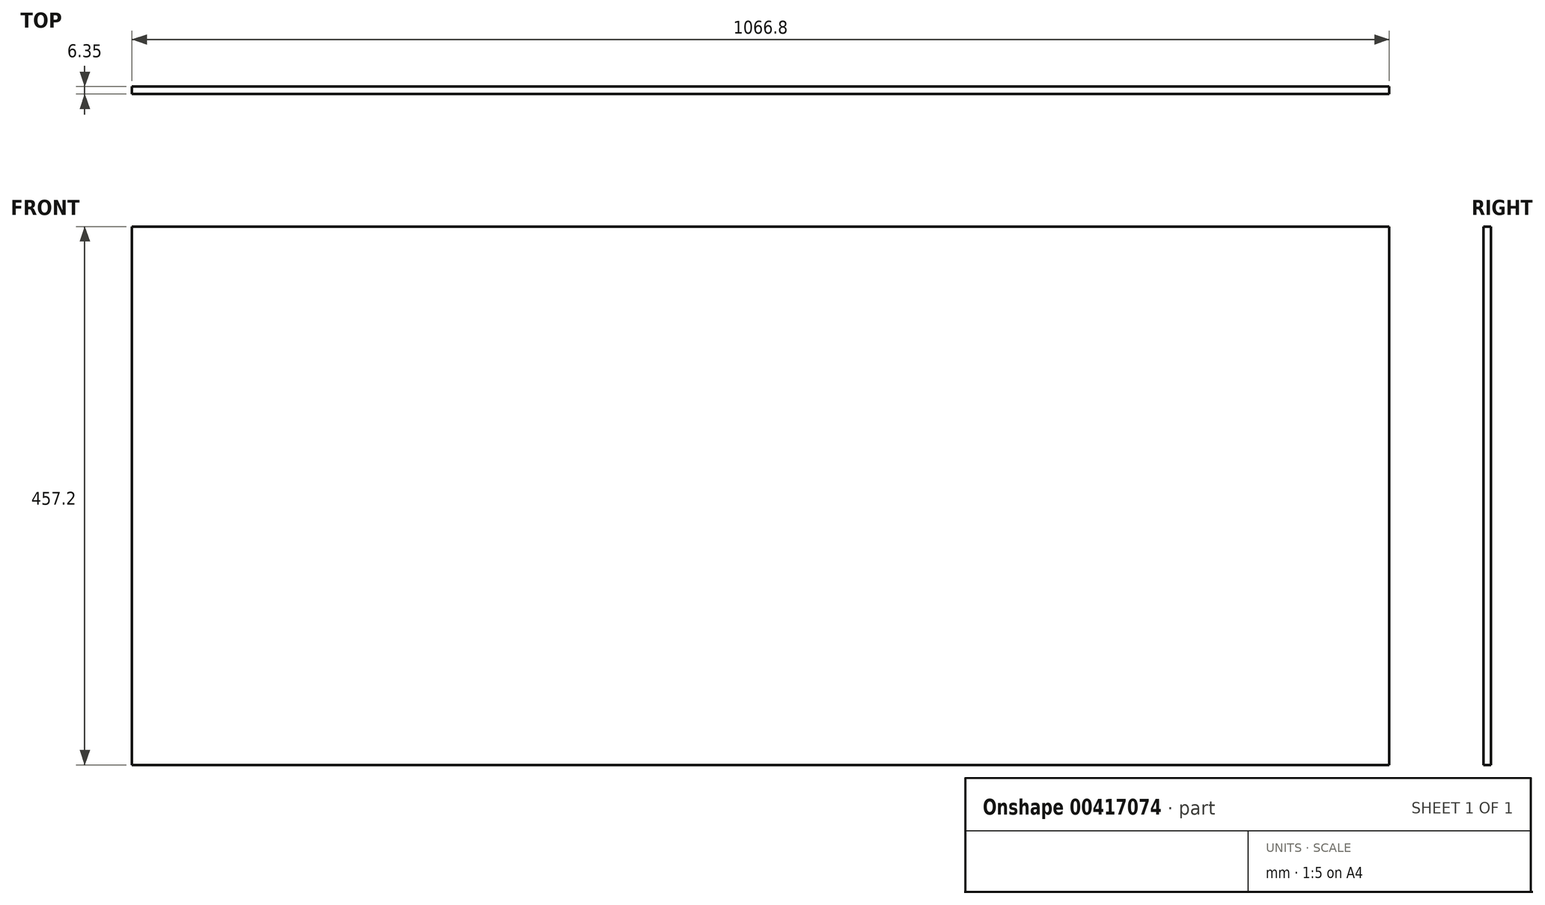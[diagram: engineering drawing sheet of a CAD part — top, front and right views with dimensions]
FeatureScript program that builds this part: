
annotation { "Feature Type Name" : "Feature", "Feature Type Description" : "" }
export const myFeature = defineFeature(function(context is Context, id is Id, definition is map)
    precondition{}
    {
        {
            var Q0;
            Q0=qCreatedBy(makeId("Front.planeOp"),FACE);
            var sketch = newSketch(context, id + "F0", { "sketchPlane" : qUnion([Q0])});
            skLineSegment(sketch, "E0.bottom", {"start": v(533.4, 228.6) * mm, "end": v(-533.4, 228.6) * mm});
            skLineSegment(sketch, "E0.top", {"start": v(533.4, -228.6) * mm, "end": v(-533.4, -228.6) * mm});
            skLineSegment(sketch, "E0.left", {"start": v(533.4, 228.6) * mm, "end": v(533.4, -228.6) * mm});
            skLineSegment(sketch, "E0.right", {"start": v(-533.4, 228.6) * mm, "end": v(-533.4, -228.6) * mm});
            skPoint(sketch, "E0.middle", {"position": v(0, 0) * mm});
            skSolve(sketch);
        }
        {
            var Q0;
            Q0=makeQuery(id+"F0.imprint","IMPRINT",FACE,{"disambiguationData":[TD([[makeQuery(id+"F0.imprint","IMPRINT",EDGE,{"derivedFrom":sQuery(id+"F0.wireOp",EDGE,"E0.bottom")}),1.0]])]});
            extrude(context, id + "F1", {"entities" : qUnion([Q0]), "depth" : 6.35 * mm, "offsetDistance" : 25.4 * mm});
        }
    });
